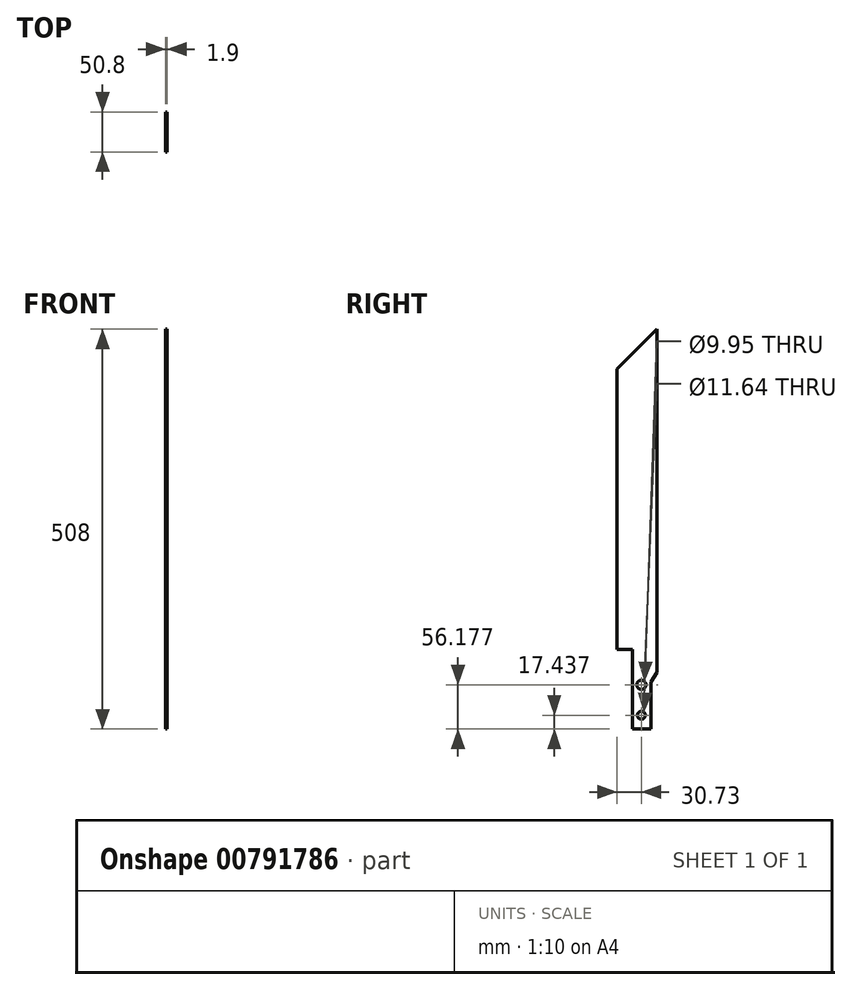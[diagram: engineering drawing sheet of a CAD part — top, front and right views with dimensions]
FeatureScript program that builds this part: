
annotation { "Feature Type Name" : "Feature", "Feature Type Description" : "" }
export const myFeature = defineFeature(function(context is Context, id is Id, definition is map)
    precondition{}
    {
        {
            var Q0;
            Q0=qCreatedBy(makeId("Right.planeOp"),FACE);
            var sketch = newSketch(context, id + "F0", { "sketchPlane" : qUnion([Q0])});
            skLineSegment(sketch, "E0", {"start": v(20.07, 205.67) * mm, "end": v(-30.73, 154.87) * mm});
            skLineSegment(sketch, "E1", {"start": v(-30.73, 154.87) * mm, "end": v(-30.73, -302.33) * mm});
            skLineSegment(sketch, "E2", {"start": v(20.07, 205.67) * mm, "end": v(20.07, -302.33) * mm});
            skLineSegment(sketch, "E3", {"start": v(20.07, -302.33) * mm, "end": v(-30.73, -302.33) * mm});
            skCircle(sketch, "E4", {"center": v(0, -284.9) * mm, "radius": 4.97 * mm});
            skCircle(sketch, "E5", {"center": v(0, -246.15) * mm, "radius": 5.82 * mm});
            skSolve(sketch);
        }
        {
            var Q0;
            Q0=qSketchRegion(id+"F0",true);
            extrude(context, id + "F1", {"entities" : qUnion([Q0]), "depth" : 1.9 * mm});
        }
        {
            var Q0;
            Q0=qSketchRegion(id+"F0",true);
            extrude(context, id + "F2", {"entities" : qUnion([Q0]), "operationType" : NewBodyOperationType.ADD, "depth" : 1.9 * mm});
        }
        {
            var Q0;
            Q0=makeQuery(id+"F1.opExtrude","CAP_FACE",FACE,{"disambiguationData":[OSD([sQuery(id+"F0.wireOp",EDGE,"E0"),sQuery(id+"F0.wireOp",EDGE,"E1"),sQuery(id+"F0.wireOp",EDGE,"E2"),sQuery(id+"F0.wireOp",EDGE,"E3"),sQuery(id+"F0.wireOp",EDGE,"E4"),sQuery(id+"F0.wireOp",EDGE,"E5")])],"isStart":false});
            var sketch = newSketch(context, id + "F3", { "sketchPlane" : qUnion([Q0])});
            skSolve(sketch);
        }
        {
            var Q0;
            Q0=makeQuery(id+"F3.imprint","IMPRINT",FACE,{"disambiguationData":[TD([[makeQuery(id+"F3.imprint","IMPRINT",EDGE,{"derivedFrom":makeQuery(id+"F1.opExtrude","CAP_EDGE",EDGE,{"disambiguationData":[OSD([sQuery(id+"F0.wireOp",EDGE,"E0")])],"isStart":false})}),1.0]])]});
            var sketch = newSketch(context, id + "F4", { "sketchPlane" : qUnion([Q0])});
            skLineSegment(sketch, "E6", {"start": v(-31.29, -233.66) * mm, "end": v(-19.98, -242.32) * mm});
            skLineSegment(sketch, "E7", {"start": v(-19.98, -303.18) * mm, "end": v(-19.98, -242.32) * mm});
            skLineSegment(sketch, "E8", {"start": v(11.95, -242.32) * mm, "end": v(11.95, -303.18) * mm});
            skLineSegment(sketch, "E9", {"start": v(11.95, -242.32) * mm, "end": v(20.93, -229.35) * mm});
            skLineSegment(sketch, "E10", {"start": v(-31.29, -233.66) * mm, "end": v(-31.29, -303.03) * mm});
            skLineSegment(sketch, "E11", {"start": v(-31.29, -303.03) * mm, "end": v(-19.98, -303.18) * mm});
            skLineSegment(sketch, "E12", {"start": v(11.95, -303.18) * mm, "end": v(20.32, -303.18) * mm});
            skLineSegment(sketch, "E13", {"start": v(20.32, -303.18) * mm, "end": v(20.93, -229.35) * mm});
            skSolve(sketch);
        }
        {
            var Q0;
            {var subQ8=sQuery(id+"F4.wireOp",EDGE,"E10");Q0=makeQuery(id+"F4.imprint","IMPRINT",FACE,{"disambiguationData":[TD([[makeQuery(id+"F4.imprint","IMPRINT",EDGE,{"derivedFrom":subQ8}),1.0]])]});}
            var Q1;
            {var subQ6=sQuery(id+"F4.wireOp",EDGE,"E12");Q1=makeQuery(id+"F4.imprint","IMPRINT",FACE,{"disambiguationData":[TD([[makeQuery(id+"F4.imprint","IMPRINT",EDGE,{"derivedFrom":subQ6}),1.0]])]});}
            var Q2;
            {var subQ0=sQuery(id+"F4.wireOp",EDGE,"E9");var subQ1=sQuery(id+"F4.wireOp",EDGE,"E8");var subQ2=makeQuery(id+"F4.imprint","INTERSECT",VERTEX,{"derivedFrom":[subQ1,subQ0]});Q2=makeQuery(id+"F4.imprint","IMPRINT",FACE,{"disambiguationData":[TD([[makeQuery(id+"F4.imprint","IMPRINT",EDGE,{"disambiguationData":[TD([[subQ2,-1.0]])],"derivedFrom":subQ1}),1.0]])]});}
            var Q3;
            {var subQ0=sQuery(id+"F4.wireOp",EDGE,"E7");var subQ1=sQuery(id+"F4.wireOp",EDGE,"E6");var subQ2=makeQuery(id+"F4.imprint","INTERSECT",VERTEX,{"derivedFrom":[subQ1,subQ0]});Q3=makeQuery(id+"F4.imprint","IMPRINT",FACE,{"disambiguationData":[TD([[makeQuery(id+"F4.imprint","IMPRINT",EDGE,{"disambiguationData":[TD([[subQ2,1.0]])],"derivedFrom":subQ1}),-1.0]])]});}
            extrude(context, id + "F5", {"entities" : qUnion([Q0, Q1, Q2, Q3]), "operationType" : NewBodyOperationType.REMOVE, "oppositeDirection" : true, "depth" : 25.4 * mm});
        }
        {
            var Q0;
            Q0=qCreatedBy(makeId("Right.planeOp"),FACE);
            var sketch = newSketch(context, id + "F6", { "sketchPlane" : qUnion([Q0])});
            skLineSegment(sketch, "E14", {"start": v(-31.95, -201.33) * mm, "end": v(-11.6, -201.33) * mm});
            skLineSegment(sketch, "E15", {"start": v(-11.6, -201.33) * mm, "end": v(-11.6, -305.1) * mm});
            skLineSegment(sketch, "E16", {"start": v(-31.95, -201.33) * mm, "end": v(-31.95, -305.1) * mm});
            skLineSegment(sketch, "E17", {"start": v(-31.95, -305.1) * mm, "end": v(-11.6, -305.1) * mm});
            skSolve(sketch);
        }
        {
            var Q0;
            Q0=qSketchRegion(id+"F6",true);
            extrude(context, id + "F7", {"entities" : qUnion([Q0]), "operationType" : NewBodyOperationType.REMOVE, "endBound" : BoundingType.THROUGH_ALL, "depth" : 25.4 * mm});
        }
    });
